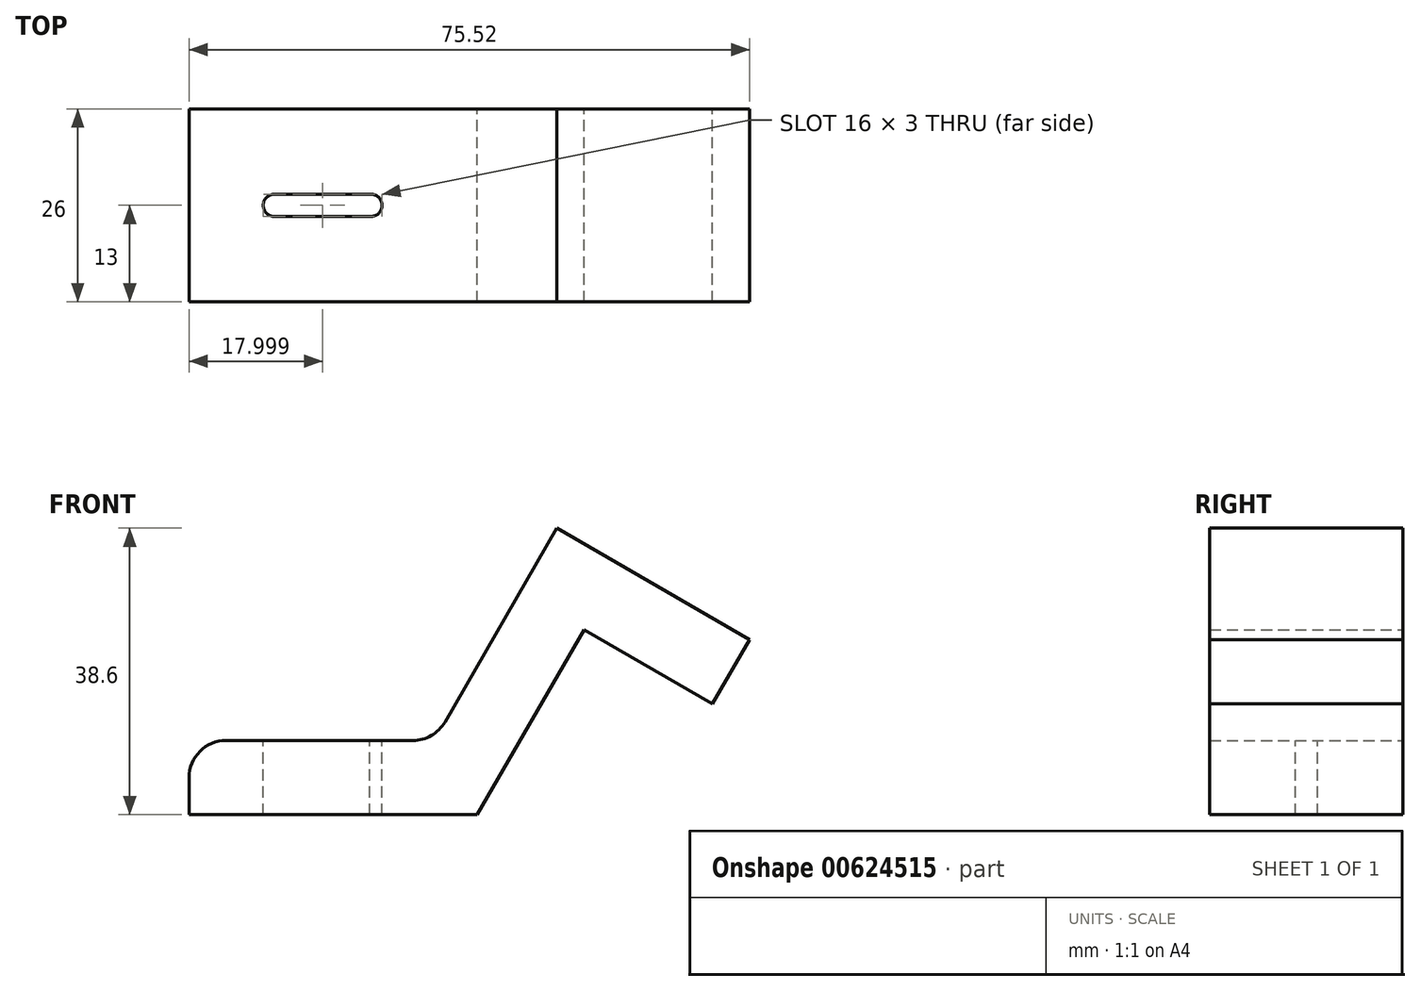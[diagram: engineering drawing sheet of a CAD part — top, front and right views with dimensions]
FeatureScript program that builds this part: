
annotation { "Feature Type Name" : "Feature", "Feature Type Description" : "" }
export const myFeature = defineFeature(function(context is Context, id is Id, definition is map)
    precondition{}
    {
        {
            var Q0;
            Q0=qCreatedBy(makeId("Front.planeOp"),FACE);
            var sketch = newSketch(context, id + "F0", { "sketchPlane" : qUnion([Q0])});
            skLineSegment(sketch, "E0", {"start": v(0, 0) * mm, "end": v(-38.8, 0) * mm});
            skLineSegment(sketch, "E1", {"start": v(0, 0) * mm, "end": v(19.4, 33.6) * mm});
            skLineSegment(sketch, "E2", {"start": v(-38.8, 0) * mm, "end": v(-38.8, 5) * mm});
            skLineSegment(sketch, "E3", {"start": v(-33.8, 10) * mm, "end": v(-8.66, 10) * mm});
            skPoint(sketch, "E4.visualSharp", {"position": v(-38.8, 10) * mm});
            skArc(sketch, "E4.filletArc", {"start": v(-33.8, 10) * mm, "mid": v(-37.34, 8.54) * mm, "end": v(-38.8, 5) * mm});
            skLineSegment(sketch, "E5", {"start": v(19.4, 33.6) * mm, "end": v(10.74, 38.6) * mm});
            skLineSegment(sketch, "E6", {"start": v(10.74, 38.6) * mm, "end": v(-4.33, 12.5) * mm});
            skPoint(sketch, "E7", {"position": v(-5.77, 10) * mm});
            skLineSegment(sketch, "E8", {"start": v(19.4, 33.6) * mm, "end": v(36.72, 23.6) * mm});
            skLineSegment(sketch, "E9", {"start": v(36.72, 23.6) * mm, "end": v(31.72, 14.94) * mm});
            skLineSegment(sketch, "E10", {"start": v(31.72, 14.94) * mm, "end": v(14.4, 24.94) * mm});
            skArc(sketch, "E11.filletArc", {"start": v(-8.66, 10) * mm, "mid": v(-6.16, 10.67) * mm, "end": v(-4.33, 12.5) * mm});
            skSolve(sketch);
        }
        {
            var Q0;
            Q0 = qSketchRegion(id + "F0", true);
            extrude(context, id + "F1", {"entities" : qUnion([Q0]), "depth" : 26 * mm, "offsetDistance" : 25 * mm});
        }
        {
            var Q0;
            Q0=makeQuery(id+"F1.opExtrude","SWEPT_FACE",FACE,{"disambiguationData":[OSD([sQuery(id+"F0.wireOp",EDGE,"E3")])]});
            var sketch = newSketch(context, id + "F2", { "sketchPlane" : qUnion([Q0])});
            skArc(sketch, "E12", {"start": v(-27.3, -11.5) * mm, "mid": v(-28.8, -13) * mm, "end": v(-27.3, -14.5) * mm});
            skPoint(sketch, "E12.centerSnap0", {"position": v(-33.8, -13) * mm});
            skArc(sketch, "E13", {"start": v(-14.48, -14.49) * mm, "mid": v(-12.8, -13.1) * mm, "end": v(-14.3, -11.5) * mm});
            skLineSegment(sketch, "E14", {"start": v(-14.48, -14.49) * mm, "end": v(-27.3, -14.5) * mm});
            skLineSegment(sketch, "E15", {"start": v(-27.3, -11.5) * mm, "end": v(-14.3, -11.5) * mm});
            skSolve(sketch);
        }
        {
            var Q0;
            Q0 = qSketchRegion(id + "F2", true);
            extrude(context, id + "F3", {"entities" : qUnion([Q0]), "operationType" : NewBodyOperationType.REMOVE, "endBound" : BoundingType.THROUGH_ALL, "oppositeDirection" : true, "depth" : 25 * mm, "offsetDistance" : 25 * mm});
        }
    });
